# Revit family: Knox1Chair001
name_source: partatom
category: Generic Models
units: mm (PartAtom-declared; Revit-internal decimal feet)

## family parameters
Always vertical = Yes
Can host rebar = No
Cut with Voids When Loaded = No
Part Type = Normal
Room Calculation Point = No
Round Connector Dimension = Use Diameter
Shared = No
Work Plane-Based = No

## types (1)
- Type1
    Arm Material = <By Category>
    Arm Outer Material = <By Category>
    Back Material = <By Category>
    Back Outer Material = <By Category>
    ClassificationName = Uniclass2015
    Default Elevation = 0"
    DurationUnit = years
    ExpectedLife = 0
    Leg Material = <By Category>
    NominalDepth = 0"
    NominalHeight = 0"
    NominalLength = 0"
    NominalWidth = 0"
    ProductionYear = 2018
    Seat Material = <By Category>
    WarrantyDurationLabor = 0
    WarrantyDurationParts = 0
    WarrantyDurationUnit = years
    _BSBibleVersion = 15
    _BimSpecGuid = 0
    _CurrentRevision = 1
    _DistributedBy = www.bimstore.co.uk

## geometry (parser evidence)
native form markers: Sweep x2
no freeform markers — native parametric forms only
